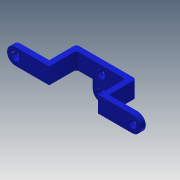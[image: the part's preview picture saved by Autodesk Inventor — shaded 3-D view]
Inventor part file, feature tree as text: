
AUTODESK INVENTOR PART (.ipt)
format: ipt  version: 2013 (Build 170138000, 138)  size: 219,136 bytes
history: native  units: mm
features: sketch x15, extrude x14, fillet x1
ambient origin geometry x8: Origin, YZ Plane, XZ Plane, XY Plane, X Axis, Y Axis, Z Axis, Center Point
bodies: Solid1 (feature_tree)
feature tree (30):
  extrude  "Extrusion1"  Depth=6.0mm
  extrude  "Extrusion2"  Depth=2.0mm
  sketch  "Sketch3"  dims[d5=2.0mm d6=10.0mm d7=0.0mm]
  extrude  "Extrusion3"  Depth=10.0mm TaperAngle=0.0deg
  extrude  "Extrusion4"  Depth=2.0mm
  sketch  "Sketch5"  dims[d10=6.0mm d11=2.0mm]
  sketch  "Sketch6"  dims[d12=14.0mm d13=0.0mm d14=14.0mm d15=0.0mm]
  extrude  "Extrusion5"  Depth=2.0mm
  extrude  "Extrusion6"  Depth=14.0mm TaperAngle=0.0deg
  extrude  "Extrusion7"  Depth=3.5mm
  extrude  "Extrusion8"  Depth=2.0mm TaperAngle=0.0deg
  fillet  "Fillet1"  Radius=3.0mm
  extrude  "Extrusion9"  Depth=3.0mm
  extrude  "Extrusion10"  Depth=1.0mm
  extrude  "Extrusion11"  Depth=3.0mm
  extrude  "Extrusion12"  Depth=6.0mm
  extrude  "Extrusion13"  Depth=3.0mm
  extrude  "Extrusion14"  Depth=2.0mm TaperAngle=0.0deg
  sketch  "Sketch15"  dims[d41=2.0mm d42=0.0mm d44=3.0mm d45=6.0mm d46=2.0mm d47=0.0mm d48=3.0mm d49=2.0mm d50=0.0mm]
  sketch  "Sketch1"  dims[d0=22.0mm d1=6.0mm]
  sketch  "Sketch2"  dims[d2=2.0mm d3=0.0mm d4=2.0mm]
  sketch  "Sketch4"  dims[d8=6.0mm d9=2.0mm]
  sketch  "Sketch7"  dims[d16=3.5mm d17=3.5mm]
  sketch  "Sketch8"  dims[d18=2.0mm d19=0.0mm d20=2.0mm d21=0.0mm d22=3.0mm]
  sketch  "Sketch9"  dims[d23=2.0mm d24=0.0mm d25=3.0mm]
  sketch  "Sketch10"  dims[d26=2.0mm d27=0.0mm d28=1.0mm]
  sketch  "Sketch11"  dims[d29=3.0mm d30=3.0mm]
  sketch  "Sketch12"  dims[d31=2.0mm d32=0.0mm d33=6.0mm]
  sketch  "Sketch13"  dims[d34=3.0mm d35=3.0mm]
  sketch  "Sketch14"  dims[d37=2.0mm d38=0.0mm d39=2.0mm d40=0.0mm]
